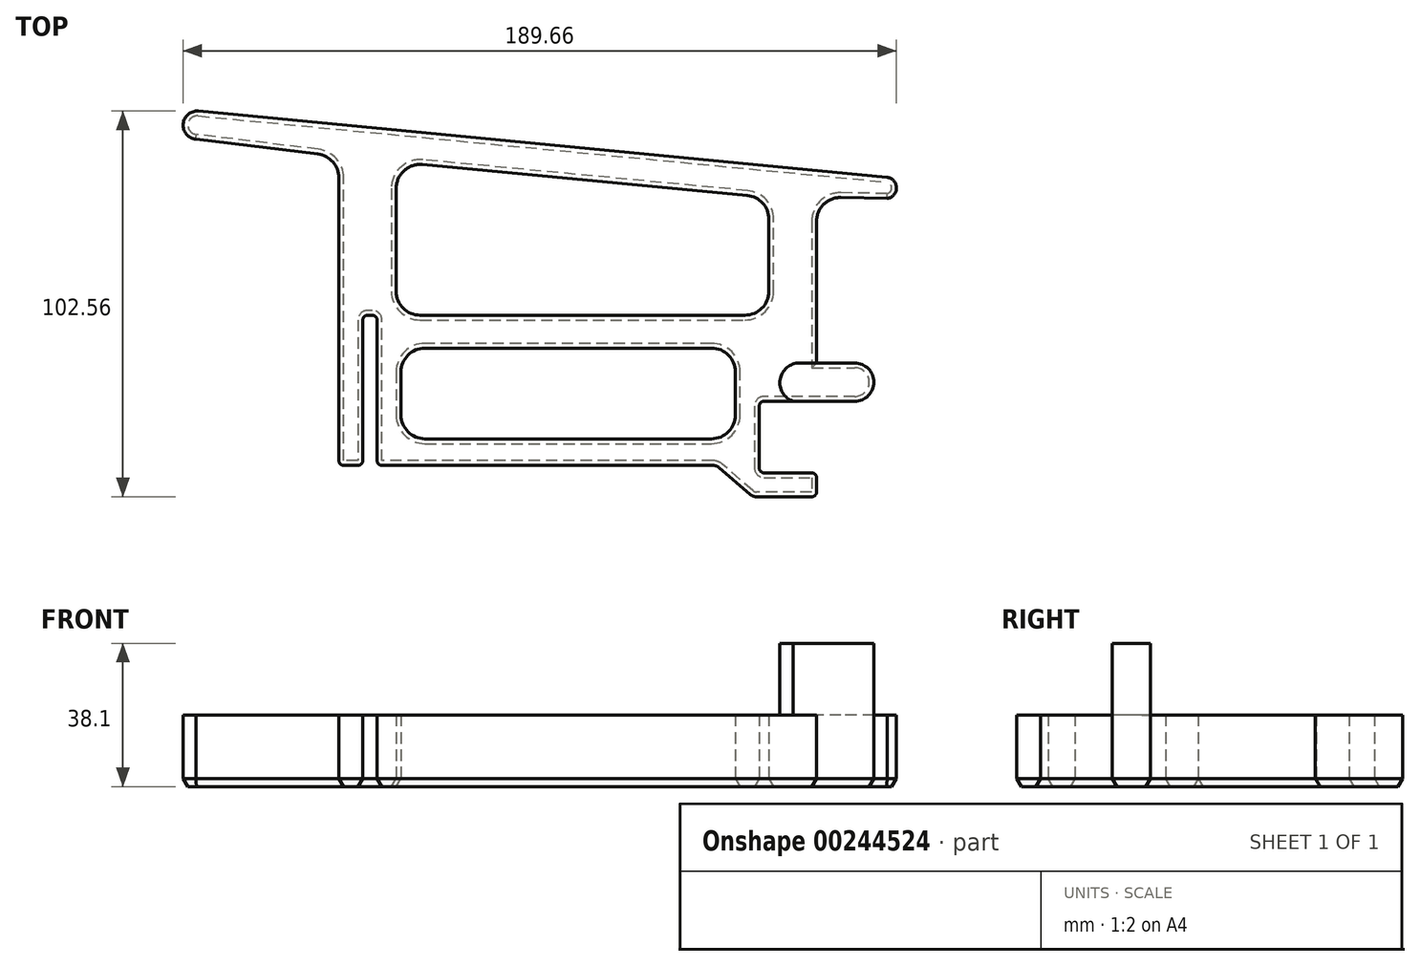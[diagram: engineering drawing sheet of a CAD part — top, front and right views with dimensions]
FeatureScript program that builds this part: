
annotation { "Feature Type Name" : "Feature", "Feature Type Description" : "" }
export const myFeature = defineFeature(function(context is Context, id is Id, definition is map)
    precondition{}
    {
        {
            var Q0;
            Q0=qCreatedBy(makeId("Top.planeOp"),FACE);
            var sketch = newSketch(context, id + "F0", { "sketchPlane" : qUnion([Q0])});
            skLineSegment(sketch, "E0", {"start": v(-47.74, -39.94) * mm, "end": v(26.7, -39.94) * mm});
            skLineSegment(sketch, "E1", {"start": v(38.22, -48.26) * mm, "end": v(52.98, -48.26) * mm});
            skLineSegment(sketch, "E2", {"start": v(54.25, -47) * mm, "end": v(54.25, -43.18) * mm});
            skLineSegment(sketch, "E3", {"start": v(52.98, -41.9) * mm, "end": v(40.28, -41.9) * mm});
            skLineSegment(sketch, "E4", {"start": v(39, -40.64) * mm, "end": v(39, -24.13) * mm});
            skLineSegment(sketch, "E5", {"start": v(40.28, -22.86) * mm, "end": v(56.8, -22.86) * mm});
            skLineSegment(sketch, "E6", {"start": v(54.25, -12.7) * mm, "end": v(54.25, 0) * mm});
            skLineSegment(sketch, "E7", {"start": v(54.25, 0) * mm, "end": v(54.25, 0) * mm});
            skLineSegment(sketch, "E8", {"start": v(54.25, 0) * mm, "end": v(54.25, 24.97) * mm});
            skLineSegment(sketch, "E9", {"start": v(41.55, 25.54) * mm, "end": v(41.55, 6.35) * mm});
            skLineSegment(sketch, "E10", {"start": v(35.2, 0) * mm, "end": v(-51.16, 0) * mm});
            skLineSegment(sketch, "E11", {"start": v(-72.75, 0) * mm, "end": v(-72.75, -24.13) * mm});
            skLineSegment(sketch, "E12", {"start": v(-66.4, -24.13) * mm, "end": v(-66.4, -1.27) * mm});
            skLineSegment(sketch, "E13", {"start": v(-72.75, 0) * mm, "end": v(-72.75, 36.56) * mm});
            skLineSegment(sketch, "E14", {"start": v(-57.51, 33.75) * mm, "end": v(-57.51, 6.35) * mm});
            skLineSegment(sketch, "E15", {"start": v(-50.56, 40.07) * mm, "end": v(35.8, 31.86) * mm});
            skLineSegment(sketch, "E16", {"start": v(-78.33, 42.86) * mm, "end": v(-110.77, 46.8) * mm});
            skLineSegment(sketch, "E17", {"start": v(-110.05, 54.28) * mm, "end": v(72.94, 36.68) * mm});
            skLineSegment(sketch, "E18", {"start": v(72.98, 31.06) * mm, "end": v(60.73, 31.32) * mm});
            skArc(sketch, "E19", {"start": v(-110.05, 54.28) * mm, "mid": v(-114.15, 50.9) * mm, "end": v(-110.77, 46.8) * mm});
            skArc(sketch, "E20", {"start": v(72.98, 31.06) * mm, "mid": v(75.5, 33.9) * mm, "end": v(72.94, 36.68) * mm});
            skLineSegment(sketch, "E21.bottom", {"start": v(-49.9, -8.74) * mm, "end": v(26.3, -8.74) * mm});
            skLineSegment(sketch, "E21.top", {"start": v(-49.9, -32.86) * mm, "end": v(26.3, -32.86) * mm});
            skLineSegment(sketch, "E21.left", {"start": v(-56.24, -15.09) * mm, "end": v(-56.24, -26.51) * mm});
            skLineSegment(sketch, "E21.right", {"start": v(32.66, -15.09) * mm, "end": v(32.66, -26.51) * mm});
            skPoint(sketch, "E22.visualSharp", {"position": v(-57.51, 40.73) * mm});
            skArc(sketch, "E22.filletArc", {"start": v(-50.56, 40.07) * mm, "mid": v(-55.43, 38.45) * mm, "end": v(-57.51, 33.75) * mm});
            skPoint(sketch, "E23.visualSharp", {"position": v(41.55, 31.32) * mm});
            skArc(sketch, "E23.filletArc", {"start": v(41.55, 25.54) * mm, "mid": v(39.9, 29.81) * mm, "end": v(35.8, 31.86) * mm});
            skPoint(sketch, "E24.visualSharp", {"position": v(41.55, 0) * mm});
            skArc(sketch, "E24.filletArc", {"start": v(35.2, 0) * mm, "mid": v(39.69, 1.86) * mm, "end": v(41.55, 6.35) * mm});
            skPoint(sketch, "E25.visualSharp", {"position": v(-57.51, 0) * mm});
            skArc(sketch, "E25.filletArc", {"start": v(-57.51, 6.35) * mm, "mid": v(-55.65, 1.86) * mm, "end": v(-51.16, 0) * mm});
            skPoint(sketch, "E26.visualSharp", {"position": v(-56.24, -8.74) * mm});
            skArc(sketch, "E26.filletArc", {"start": v(-49.9, -8.74) * mm, "mid": v(-54.38, -10.6) * mm, "end": v(-56.24, -15.09) * mm});
            skPoint(sketch, "E27.visualSharp", {"position": v(32.66, -8.74) * mm});
            skArc(sketch, "E27.filletArc", {"start": v(32.66, -15.09) * mm, "mid": v(30.8, -10.6) * mm, "end": v(26.3, -8.74) * mm});
            skPoint(sketch, "E28.visualSharp", {"position": v(32.66, -32.86) * mm});
            skArc(sketch, "E28.filletArc", {"start": v(26.3, -32.86) * mm, "mid": v(30.8, -31) * mm, "end": v(32.66, -26.51) * mm});
            skPoint(sketch, "E29.visualSharp", {"position": v(-56.24, -32.86) * mm});
            skArc(sketch, "E29.filletArc", {"start": v(-56.24, -26.51) * mm, "mid": v(-54.38, -31) * mm, "end": v(-49.9, -32.86) * mm});
            skPoint(sketch, "E30.visualSharp", {"position": v(-54.09, -39.94) * mm});
            skPoint(sketch, "E31.visualSharp", {"position": v(-72.75, 42.18) * mm});
            skArc(sketch, "E31.filletArc", {"start": v(-72.75, 36.56) * mm, "mid": v(-74.35, 40.77) * mm, "end": v(-78.33, 42.86) * mm});
            skPoint(sketch, "E32.visualSharp", {"position": v(54.25, 31.45) * mm});
            skArc(sketch, "E32.filletArc", {"start": v(60.73, 31.32) * mm, "mid": v(56.16, 29.5) * mm, "end": v(54.25, 24.97) * mm});
            skPoint(sketch, "E33.visualSharp", {"position": v(-66.4, -25.4) * mm});
            skPoint(sketch, "E34.visualSharp", {"position": v(-72.75, -25.4) * mm});
            skPoint(sketch, "E35.visualSharp", {"position": v(-66.4, 0) * mm});
            skArc(sketch, "E35.filletArc", {"start": v(-65.13, 0) * mm, "mid": v(-66.03, -0.37) * mm, "end": v(-66.4, -1.27) * mm});
            skPoint(sketch, "E36.visualSharp", {"position": v(-62.6, 0) * mm});
            skPoint(sketch, "E37.visualSharp", {"position": v(-56.24, -25.4) * mm});
            skPoint(sketch, "E38.visualSharp", {"position": v(34.81, -39.94) * mm});
            skPoint(sketch, "E39.visualSharp", {"position": v(36.47, -48.26) * mm});
            skPoint(sketch, "E40.visualSharp", {"position": v(54.25, -48.26) * mm});
            skArc(sketch, "E40.filletArc", {"start": v(52.98, -48.26) * mm, "mid": v(53.88, -47.89) * mm, "end": v(54.25, -47) * mm});
            skPoint(sketch, "E41.visualSharp", {"position": v(54.25, -41.9) * mm});
            skArc(sketch, "E41.filletArc", {"start": v(54.25, -43.18) * mm, "mid": v(53.88, -42.28) * mm, "end": v(52.98, -41.9) * mm});
            skPoint(sketch, "E42.visualSharp", {"position": v(39, -41.9) * mm});
            skArc(sketch, "E42.filletArc", {"start": v(39, -40.64) * mm, "mid": v(39.38, -41.54) * mm, "end": v(40.28, -41.91) * mm});
            skPoint(sketch, "E43.visualSharp", {"position": v(39, -22.86) * mm});
            skArc(sketch, "E43.filletArc", {"start": v(40.28, -22.86) * mm, "mid": v(39.38, -23.23) * mm, "end": v(39, -24.13) * mm});
            skPoint(sketch, "E44.visualSharp", {"position": v(54.25, -22.86) * mm});
            skLineSegment(sketch, "E45", {"start": v(-62.6, -24.13) * mm, "end": v(-62.6, -38.67) * mm});
            skLineSegment(sketch, "E46", {"start": v(-47.74, -39.94) * mm, "end": v(-61.32, -39.94) * mm});
            skLineSegment(sketch, "E47", {"start": v(-72.75, -24.13) * mm, "end": v(-72.75, -38.67) * mm});
            skLineSegment(sketch, "E48", {"start": v(-66.4, -24.13) * mm, "end": v(-66.4, -38.67) * mm});
            skLineSegment(sketch, "E49.trimOffspring", {"start": v(-67.67, -39.94) * mm, "end": v(-71.48, -39.94) * mm});
            skPoint(sketch, "E50.visualSharp", {"position": v(-72.75, -39.94) * mm});
            skArc(sketch, "E50.filletArc", {"start": v(-72.75, -38.67) * mm, "mid": v(-72.38, -39.56) * mm, "end": v(-71.48, -39.94) * mm});
            skPoint(sketch, "E51.visualSharp", {"position": v(-66.4, -39.94) * mm});
            skArc(sketch, "E51.filletArc", {"start": v(-67.67, -39.94) * mm, "mid": v(-66.77, -39.56) * mm, "end": v(-66.4, -38.67) * mm});
            skPoint(sketch, "E52.visualSharp", {"position": v(-62.6, -39.94) * mm});
            skArc(sketch, "E52.filletArc", {"start": v(-62.6, -38.67) * mm, "mid": v(-62.22, -39.56) * mm, "end": v(-61.32, -39.94) * mm});
            skLineSegment(sketch, "E53", {"start": v(36.55, -47.64) * mm, "end": v(28.36, -40.55) * mm});
            skPoint(sketch, "E54.visualSharp", {"position": v(27.64, -39.94) * mm});
            skArc(sketch, "E54.filletArc", {"start": v(28.36, -40.55) * mm, "mid": v(27.58, -40.1) * mm, "end": v(26.7, -39.94) * mm});
            skPoint(sketch, "E55.visualSharp", {"position": v(37.27, -48.26) * mm});
            skArc(sketch, "E55.filletArc", {"start": v(36.55, -47.64) * mm, "mid": v(37.33, -48.1) * mm, "end": v(38.22, -48.26) * mm});
            skLineSegment(sketch, "E56", {"start": v(-60.68, 0) * mm, "end": v(-60.68, 49.53) * mm, "construction": true});
            skLineSegment(sketch, "E57", {"start": v(56.8, -22.86) * mm, "end": v(64.4, -22.86) * mm});
            skLineSegment(sketch, "E58", {"start": v(64.4, -12.7) * mm, "end": v(54.25, -12.7) * mm});
            skArc(sketch, "E59", {"start": v(64.4, -22.86) * mm, "mid": v(69.49, -17.78) * mm, "end": v(64.4, -12.7) * mm});
            skLineSegment(sketch, "E60", {"start": v(-62.6, -24.13) * mm, "end": v(-62.6, -1.27) * mm});
            skLineSegment(sketch, "E61", {"start": v(-65.13, 0) * mm, "end": v(-63.86, 0) * mm});
            skArc(sketch, "E62.filletArc", {"start": v(-62.6, -1.27) * mm, "mid": v(-62.96, -0.37) * mm, "end": v(-63.86, 0) * mm});
            skSolve(sketch);
        }
        {
            var Q0;
            Q0=qSketchRegion(id+"F0",true);
            extrude(context, id + "F1", {"entities" : qUnion([Q0]), "depth" : 19.05 * mm});
        }
        {
            var Q0;
            Q0=makeQuery(id+"F1.opExtrude","CAP_FACE",FACE,{"disambiguationData":[OSD([sQuery(id+"F0.wireOp",EDGE,"WzjgW17k-lggf-UnH0-HMgM-pe6naiI595cO"),sQuery(id+"F0.wireOp",EDGE,"9XZd8n2k-COVL-yRkC-SFTw-dNNrleFXtEeW"),sQuery(id+"F0.wireOp",EDGE,"E0"),sQuery(id+"F0.wireOp",EDGE,"E1"),sQuery(id+"F0.wireOp",EDGE,"E2"),sQuery(id+"F0.wireOp",EDGE,"E3"),sQuery(id+"F0.wireOp",EDGE,"E4"),sQuery(id+"F0.wireOp",EDGE,"E5"),sQuery(id+"F0.wireOp",EDGE,"E6"),sQuery(id+"F0.wireOp",EDGE,"E8"),sQuery(id+"F0.wireOp",EDGE,"E9"),sQuery(id+"F0.wireOp",EDGE,"E10"),sQuery(id+"F0.wireOp",EDGE,"E11"),sQuery(id+"F0.wireOp",EDGE,"E12"),sQuery(id+"F0.wireOp",EDGE,"E13"),sQuery(id+"F0.wireOp",EDGE,"E14"),sQuery(id+"F0.wireOp",EDGE,"E15"),sQuery(id+"F0.wireOp",EDGE,"E16"),sQuery(id+"F0.wireOp",EDGE,"E17"),sQuery(id+"F0.wireOp",EDGE,"E18"),sQuery(id+"F0.wireOp",EDGE,"E19"),sQuery(id+"F0.wireOp",EDGE,"E20"),sQuery(id+"F0.wireOp",EDGE,"E21.bottom"),sQuery(id+"F0.wireOp",EDGE,"E21.top"),sQuery(id+"F0.wireOp",EDGE,"E21.left"),sQuery(id+"F0.wireOp",EDGE,"E21.right"),sQuery(id+"F0.wireOp",EDGE,"E22.filletArc"),sQuery(id+"F0.wireOp",EDGE,"E23.filletArc"),sQuery(id+"F0.wireOp",EDGE,"E24.filletArc"),sQuery(id+"F0.wireOp",EDGE,"E25.filletArc"),sQuery(id+"F0.wireOp",EDGE,"E26.filletArc"),sQuery(id+"F0.wireOp",EDGE,"E27.filletArc"),sQuery(id+"F0.wireOp",EDGE,"E28.filletArc"),sQuery(id+"F0.wireOp",EDGE,"E29.filletArc"),sQuery(id+"F0.wireOp",EDGE,"E31.filletArc"),sQuery(id+"F0.wireOp",EDGE,"E32.filletArc"),sQuery(id+"F0.wireOp",EDGE,"E35.filletArc"),sQuery(id+"F0.wireOp",EDGE,"E36.filletArc"),sQuery(id+"F0.wireOp",EDGE,"E40.filletArc"),sQuery(id+"F0.wireOp",EDGE,"E41.filletArc"),sQuery(id+"F0.wireOp",EDGE,"E42.filletArc"),sQuery(id+"F0.wireOp",EDGE,"E43.filletArc"),sQuery(id+"F0.wireOp",EDGE,"E45"),sQuery(id+"F0.wireOp",EDGE,"E46"),sQuery(id+"F0.wireOp",EDGE,"E47"),sQuery(id+"F0.wireOp",EDGE,"E48"),sQuery(id+"F0.wireOp",EDGE,"E49.trimOffspring"),sQuery(id+"F0.wireOp",EDGE,"E50.filletArc"),sQuery(id+"F0.wireOp",EDGE,"E51.filletArc"),sQuery(id+"F0.wireOp",EDGE,"E52.filletArc"),sQuery(id+"F0.wireOp",EDGE,"E53"),sQuery(id+"F0.wireOp",EDGE,"E54.filletArc"),sQuery(id+"F0.wireOp",EDGE,"E55.filletArc"),sQuery(id+"F0.wireOp",EDGE,"E57"),sQuery(id+"F0.wireOp",EDGE,"E58"),sQuery(id+"F0.wireOp",EDGE,"E59")])],"isStart":true});
            var sketch = newSketch(context, id + "F2", { "sketchPlane" : qUnion([Q0])});
            skLineSegment(sketch, "E63.bottom", {"start": v(48.01, 22.86) * mm, "end": v(64.4, 22.86) * mm});
            skLineSegment(sketch, "E63.top", {"start": v(49.7, 12.7) * mm, "end": v(64.4, 12.7) * mm});
            skArc(sketch, "E64", {"start": v(64.4, 12.7) * mm, "mid": v(69.49, 17.78) * mm, "end": v(64.4, 22.86) * mm});
            skArc(sketch, "E65", {"start": v(48.01, 22.86) * mm, "mid": v(44.55, 17.06) * mm, "end": v(49.7, 12.7) * mm});
            skSolve(sketch);
        }
        {
            var Q0;
            Q0=qSketchRegion(id+"F2",true);
            extrude(context, id + "F3", {"entities" : qUnion([Q0]), "operationType" : NewBodyOperationType.ADD, "oppositeDirection" : true, "depth" : 38.1 * mm});
        }
        {
            var Q0;
            Q0=makeQuery(id+"F1.opExtrude","CAP_FACE",FACE,{"disambiguationData":[OSD([sQuery(id+"F0.wireOp",EDGE,"E0"),sQuery(id+"F0.wireOp",EDGE,"E1"),sQuery(id+"F0.wireOp",EDGE,"E2"),sQuery(id+"F0.wireOp",EDGE,"E3"),sQuery(id+"F0.wireOp",EDGE,"E4"),sQuery(id+"F0.wireOp",EDGE,"E5"),sQuery(id+"F0.wireOp",EDGE,"E6"),sQuery(id+"F0.wireOp",EDGE,"E8"),sQuery(id+"F0.wireOp",EDGE,"E9"),sQuery(id+"F0.wireOp",EDGE,"E10"),sQuery(id+"F0.wireOp",EDGE,"E11"),sQuery(id+"F0.wireOp",EDGE,"E12"),sQuery(id+"F0.wireOp",EDGE,"E13"),sQuery(id+"F0.wireOp",EDGE,"E14"),sQuery(id+"F0.wireOp",EDGE,"E15"),sQuery(id+"F0.wireOp",EDGE,"E16"),sQuery(id+"F0.wireOp",EDGE,"E17"),sQuery(id+"F0.wireOp",EDGE,"E18"),sQuery(id+"F0.wireOp",EDGE,"E19"),sQuery(id+"F0.wireOp",EDGE,"E20"),sQuery(id+"F0.wireOp",EDGE,"E21.bottom"),sQuery(id+"F0.wireOp",EDGE,"E21.top"),sQuery(id+"F0.wireOp",EDGE,"E21.left"),sQuery(id+"F0.wireOp",EDGE,"E21.right"),sQuery(id+"F0.wireOp",EDGE,"E22.filletArc"),sQuery(id+"F0.wireOp",EDGE,"E23.filletArc"),sQuery(id+"F0.wireOp",EDGE,"E24.filletArc"),sQuery(id+"F0.wireOp",EDGE,"E25.filletArc"),sQuery(id+"F0.wireOp",EDGE,"E26.filletArc"),sQuery(id+"F0.wireOp",EDGE,"E27.filletArc"),sQuery(id+"F0.wireOp",EDGE,"E28.filletArc"),sQuery(id+"F0.wireOp",EDGE,"E29.filletArc"),sQuery(id+"F0.wireOp",EDGE,"E31.filletArc"),sQuery(id+"F0.wireOp",EDGE,"E32.filletArc"),sQuery(id+"F0.wireOp",EDGE,"E35.filletArc"),sQuery(id+"F0.wireOp",EDGE,"E40.filletArc"),sQuery(id+"F0.wireOp",EDGE,"E41.filletArc"),sQuery(id+"F0.wireOp",EDGE,"E42.filletArc"),sQuery(id+"F0.wireOp",EDGE,"E43.filletArc"),sQuery(id+"F0.wireOp",EDGE,"E45"),sQuery(id+"F0.wireOp",EDGE,"E46"),sQuery(id+"F0.wireOp",EDGE,"E47"),sQuery(id+"F0.wireOp",EDGE,"E48"),sQuery(id+"F0.wireOp",EDGE,"E49.trimOffspring"),sQuery(id+"F0.wireOp",EDGE,"E50.filletArc"),sQuery(id+"F0.wireOp",EDGE,"E51.filletArc"),sQuery(id+"F0.wireOp",EDGE,"E52.filletArc"),sQuery(id+"F0.wireOp",EDGE,"E53"),sQuery(id+"F0.wireOp",EDGE,"E54.filletArc"),sQuery(id+"F0.wireOp",EDGE,"E55.filletArc"),sQuery(id+"F0.wireOp",EDGE,"E57"),sQuery(id+"F0.wireOp",EDGE,"E58"),sQuery(id+"F0.wireOp",EDGE,"E59"),sQuery(id+"F0.wireOp",EDGE,"E60"),sQuery(id+"F0.wireOp",EDGE,"E61"),sQuery(id+"F0.wireOp",EDGE,"E62.filletArc")])],"isStart":true});
            chamfer(context, id + "F4", {"entities" : qUnion([Q0]), "chamferType" : ChamferType.OFFSET_ANGLE, "width" : 1.27 * mm, "oppositeDirection" : false, "angle" : 60 * degree, "tangentPropagation" : true});
        }
    });
